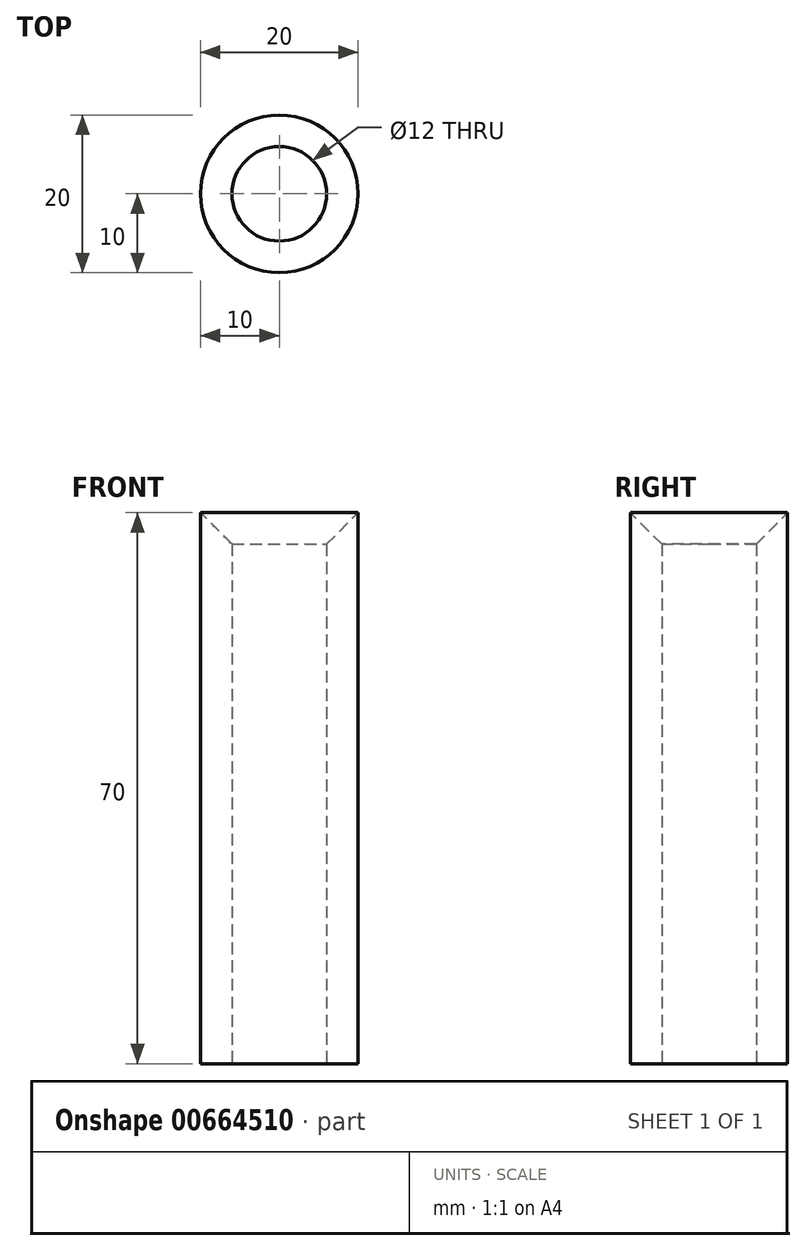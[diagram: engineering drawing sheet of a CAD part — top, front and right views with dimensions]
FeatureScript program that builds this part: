
annotation { "Feature Type Name" : "Feature", "Feature Type Description" : "" }
export const myFeature = defineFeature(function(context is Context, id is Id, definition is map)
    precondition{}
    {
        {
            var Q0;
            Q0=qCreatedBy(makeId("Top.planeOp"),FACE);
            var sketch = newSketch(context, id + "F0", { "sketchPlane" : qUnion([Q0])});
            skCircle(sketch, "E0", {"center": v(0, 0) * mm, "radius": 10 * mm});
            skSolve(sketch);
        }
        {
            var Q0;
            Q0 = qSketchRegion(id + "F0", true);
            extrude(context, id + "F1", {"entities" : qUnion([Q0]), "depth" : 70 * mm, "offsetDistance" : 25 * mm});
        }
        {
            var Q0;
            Q0=makeQuery(id+"F1.opExtrude","CAP_FACE",FACE,{"disambiguationData":[OSD([sQuery(id+"F0.wireOp",EDGE,"E0")])],"isStart":false});
            var sketch = newSketch(context, id + "F2", { "sketchPlane" : qUnion([Q0])});
            skCircle(sketch, "E1", {"center": v(0, 0) * mm, "radius": 6 * mm});
            skSolve(sketch);
        }
        {
            var Q0;
            Q0=sQuery(id+"F2.wireOp",VERTEX,"E1.center");
            var Q1;
            Q1=makeQuery(id+"F1.opExtrude","SWEPT_BODY",BODY,{"disambiguationData":[OSD([sQuery(id+"F0.wireOp",EDGE,"E0")])]});
            hole(context, id + "F3", {"style" : HoleStyle.C_SINK, "endStyle" : HoleEndStyle.THROUGH, "holeDiameter" : 12 * mm, "cSinkDiameter" : 20 * mm, "cSinkAngle" : 90 * degree, "majorDiameter" : 5 * mm, "isTappedThrough" : true, "tappedDepth" : 12 * mm, "tapClearance" : 3, "locations" : qUnion([Q0]), "scope" : qUnion([Q1])});
        }
    });
